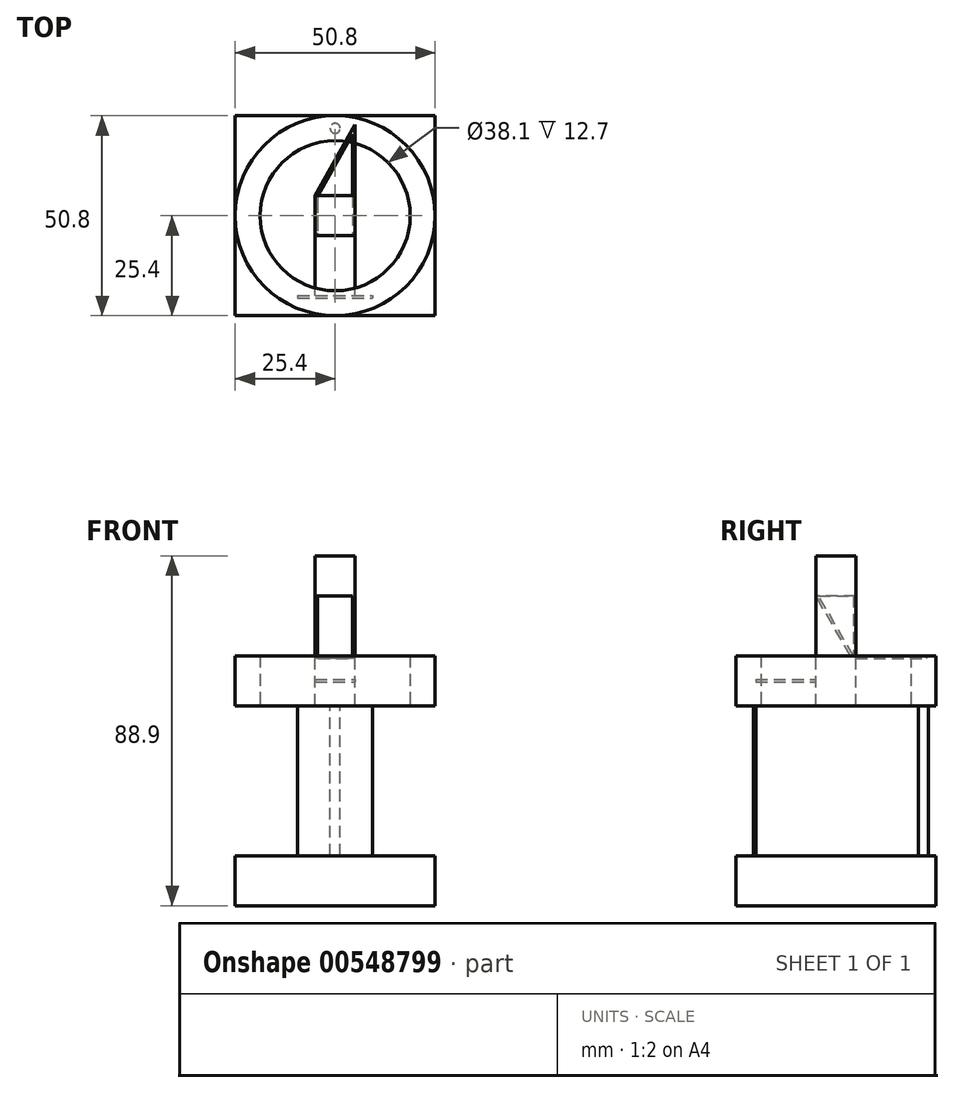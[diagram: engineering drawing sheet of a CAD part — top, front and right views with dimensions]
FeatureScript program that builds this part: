
annotation { "Feature Type Name" : "Feature", "Feature Type Description" : "" }
export const myFeature = defineFeature(function(context is Context, id is Id, definition is map)
    precondition{}
    {
        {
            var Q0;
            Q0=qCreatedBy(makeId("Top.planeOp"),FACE);
            var sketch = newSketch(context, id + "F0", { "sketchPlane" : qUnion([Q0])});
            skLineSegment(sketch, "E0.bottom", {"start": v(-25.4, 25.4) * mm, "end": v(25.4, 25.4) * mm});
            skLineSegment(sketch, "E0.top", {"start": v(-25.4, -25.4) * mm, "end": v(25.4, -25.4) * mm});
            skLineSegment(sketch, "E0.left", {"start": v(-25.4, 25.4) * mm, "end": v(-25.4, -25.4) * mm});
            skLineSegment(sketch, "E0.right", {"start": v(25.4, 25.4) * mm, "end": v(25.4, -25.4) * mm});
            skLineSegment(sketch, "E1", {"start": v(-25.4, -25.4) * mm, "end": v(25.4, 25.4) * mm, "construction": true});
            skSolve(sketch);
        }
        {
            var Q0;
            Q0 = qSketchRegion(id + "F0", true);
            extrude(context, id + "F1", {"entities" : qUnion([Q0]), "depth" : 12.7 * mm, "offsetDistance" : 25.4 * mm});
        }
        {
            var Q0;
            Q0=qCreatedBy(makeId("Top.planeOp"),FACE);
            var sketch = newSketch(context, id + "F2", { "sketchPlane" : qUnion([Q0])});
            skCircle(sketch, "E2", {"center": v(0, 0) * mm, "radius": 25.4 * mm});
            skCircle(sketch, "E3", {"center": v(0, 0) * mm, "radius": 19.05 * mm});
            skSolve(sketch);
        }
        {
            var Q0;
            Q0 = qSketchRegion(id + "F2", true);
            extrude(context, id + "F3", {"entities" : qUnion([Q0]), "operationType" : NewBodyOperationType.ADD, "depth" : 63.5 * mm, "offsetDistance" : 25.4 * mm});
        }
        {
            var Q0;
            Q0=qCreatedBy(makeId("Front.planeOp"),FACE);
            var sketch = newSketch(context, id + "F4", { "sketchPlane" : qUnion([Q0])});
            skLineSegment(sketch, "E4.bottom", {"start": v(35.21, 50.8) * mm, "end": v(-40.99, 50.8) * mm});
            skLineSegment(sketch, "E4.top", {"start": v(35.21, 12.7) * mm, "end": v(-40.99, 12.7) * mm});
            skLineSegment(sketch, "E4.left", {"start": v(35.21, 50.8) * mm, "end": v(35.21, 12.7) * mm});
            skLineSegment(sketch, "E4.right", {"start": v(-40.99, 50.8) * mm, "end": v(-40.99, 12.7) * mm});
            skSolve(sketch);
        }
        {
            var Q0;
            Q0 = qSketchRegion(id + "F4", true);
            extrude(context, id + "F5", {"entities" : qUnion([Q0]), "operationType" : NewBodyOperationType.REMOVE, "endBound" : BoundingType.THROUGH_ALL, "depth" : 25.4 * mm, "offsetDistance" : 25.4 * mm, "hasSecondDirection" : true, "secondDirectionBound" : SecondDirectionBoundingType.THROUGH_ALL, "secondDirectionOppositeDirection" : true, "secondDirectionDepth" : 25.4 * mm});
        }
        {
            var Q0;
            Q0=makeQuery(id+"F5.boolean.opBoolean","COPY",FACE,{"derivedFrom":makeQuery(id+"F5.opExtrude","SWEPT_FACE",FACE,{"disambiguationData":[OSD([sQuery(id+"F4.wireOp",EDGE,"E4.bottom")])]})});
            var sketch = newSketch(context, id + "F6", { "sketchPlane" : qUnion([Q0])});
            skPoint(sketch, "E5", {"position": v(0, 0) * mm});
            skCircle(sketch, "E6", {"center": v(0, -22.23) * mm, "radius": 1.27 * mm});
            skLineSegment(sketch, "E7.bottom", {"start": v(9.53, 20.96) * mm, "end": v(-9.53, 20.96) * mm});
            skLineSegment(sketch, "E7.top", {"start": v(9.53, 20.32) * mm, "end": v(-9.53, 20.32) * mm});
            skLineSegment(sketch, "E7.left", {"start": v(9.52, 20.96) * mm, "end": v(9.52, 20.32) * mm});
            skLineSegment(sketch, "E7.right", {"start": v(-9.53, 20.96) * mm, "end": v(-9.53, 20.32) * mm});
            skLineSegment(sketch, "E8", {"start": v(0, 20.32) * mm, "end": v(0, 0) * mm, "construction": true});
            skSolve(sketch);
        }
        {
            var Q0;
            Q0 = qSketchRegion(id + "F6", true);
            var Q1;
            {var subQ0=sQuery(id+"F0.wireOp",EDGE,"E0.right");var subQ1=sQuery(id+"F0.wireOp",EDGE,"E0.left");var subQ2=sQuery(id+"F0.wireOp",EDGE,"E0.top");var subQ3=sQuery(id+"F0.wireOp",EDGE,"E0.bottom");var subQ4=makeQuery(id+"F1.opExtrude","CAP_FACE",FACE,{"disambiguationData":[OSD([subQ3,subQ2,subQ1,subQ0])],"isStart":false});var subQ5=makeQuery(id+"F1.opExtrude","SWEPT_FACE",FACE,{"disambiguationData":[OSD([subQ2])]});var subQ6=makeQuery(id+"F3.opExtrude","SWEPT_FACE",FACE,{"disambiguationData":[OSD([sQuery(id+"F2.wireOp",EDGE,"E2")])]});var subQ7=makeQuery(id+"F1.opExtrude","SWEPT_FACE",FACE,{"disambiguationData":[OSD([subQ0])]});var subQ8=makeQuery(id+"F1.opExtrude","SWEPT_FACE",FACE,{"disambiguationData":[OSD([subQ1])]});var subQ9=makeQuery(id+"F1.opExtrude","SWEPT_FACE",FACE,{"disambiguationData":[OSD([subQ3])]});Q1=makeQuery(id+"F5.boolean.opBoolean","MERGE",FACE,{"derivedFrom":[makeQuery(id+"F3.boolean.opBoolean","SPLIT",FACE,{"disambiguationData":[TD([makeQuery(id+"F3.opExtrude","SWEPT_FACE",FACE,{"disambiguationData":[OSD([sQuery(id+"F2.wireOp",EDGE,"E3")])]})])],"derivedFrom":subQ4}),makeQuery(id+"F3.boolean.opBoolean","SPLIT",FACE,{"disambiguationData":[TD([subQ9,subQ4,subQ8,subQ6])],"derivedFrom":subQ4}),makeQuery(id+"F3.boolean.opBoolean","SPLIT",FACE,{"disambiguationData":[TD([subQ9,subQ4,subQ7,subQ6])],"derivedFrom":subQ4}),makeQuery(id+"F3.boolean.opBoolean","SPLIT",FACE,{"disambiguationData":[TD([subQ4,subQ5,subQ8,subQ6])],"derivedFrom":subQ4}),makeQuery(id+"F3.boolean.opBoolean","SPLIT",FACE,{"disambiguationData":[TD([subQ4,subQ5,subQ7,subQ6])],"derivedFrom":subQ4}),makeQuery(id+"F5.opExtrude","SWEPT_FACE",FACE,{"disambiguationData":[OSD([sQuery(id+"F4.wireOp",EDGE,"E4.top")])]})]});}
            extrude(context, id + "F7", {"entities" : qUnion([Q0]), "endBound" : BoundingType.UP_TO_SURFACE, "depth" : 25.4 * mm, "endBoundEntityFace" : qUnion([Q1]), "offsetDistance" : 25.4 * mm});
        }
        {
            var Q0;
            Q0=makeQuery(id+"F3.opExtrude","CAP_FACE",FACE,{"disambiguationData":[OSD([sQuery(id+"F2.wireOp",EDGE,"E2"),sQuery(id+"F2.wireOp",EDGE,"E3")])],"isStart":false});
            var sketch = newSketch(context, id + "F8", { "sketchPlane" : qUnion([Q0])});
            skLineSegment(sketch, "E9.bottom", {"start": v(-5.08, 5.08) * mm, "end": v(5.08, 5.08) * mm});
            skLineSegment(sketch, "E9.top", {"start": v(-5.08, -5.08) * mm, "end": v(5.08, -5.08) * mm});
            skLineSegment(sketch, "E9.left", {"start": v(-5.08, 5.08) * mm, "end": v(-5.08, -5.08) * mm});
            skLineSegment(sketch, "E9.right", {"start": v(5.08, 5.08) * mm, "end": v(5.08, -5.08) * mm});
            skLineSegment(sketch, "E10", {"start": v(-5.08, -5.08) * mm, "end": v(5.08, 5.08) * mm, "construction": true});
            skSolve(sketch);
        }
        {
            var Q0;
            Q0 = qSketchRegion(id + "F8", true);
            extrude(context, id + "F9", {"entities" : qUnion([Q0]), "oppositeDirection" : true, "depth" : 12.7 * mm, "offsetDistance" : 25.4 * mm, "hasSecondDirection" : true, "secondDirectionOppositeDirection" : false, "secondDirectionDepth" : 25.4 * mm});
        }
        {
            var Q0;
            Q0=makeQuery(id+"F9.opExtrude","SWEPT_FACE",FACE,{"disambiguationData":[OSD([sQuery(id+"F8.wireOp",EDGE,"E9.right")])]});
            var sketch = newSketch(context, id + "F10", { "sketchPlane" : qUnion([Q0])});
            skLineSegment(sketch, "E11.bottom", {"start": v(-20.32, 57.47) * mm, "end": v(-5.08, 57.47) * mm});
            skLineSegment(sketch, "E11.top", {"start": v(-20.32, 56.83) * mm, "end": v(-5.08, 56.83) * mm});
            skLineSegment(sketch, "E11.left", {"start": v(-20.32, 57.47) * mm, "end": v(-20.32, 56.83) * mm});
            skLineSegment(sketch, "E11.right", {"start": v(-5.08, 57.47) * mm, "end": v(-5.08, 56.83) * mm});
            skLineSegment(sketch, "E12", {"start": v(-5.08, 57.15) * mm, "end": v(-5.08, 50.8) * mm, "construction": true});
            skSolve(sketch);
        }
        {
            var Q0;
            Q0 = qSketchRegion(id + "F10", true);
            var Q1;
            Q1=makeQuery(id+"F9.opExtrude","SWEPT_FACE",FACE,{"disambiguationData":[OSD([sQuery(id+"F8.wireOp",EDGE,"E9.left")])]});
            extrude(context, id + "F11", {"entities" : qUnion([Q0]), "endBound" : BoundingType.UP_TO_SURFACE, "oppositeDirection" : true, "depth" : 25.4 * mm, "endBoundEntityFace" : qUnion([Q1]), "offsetDistance" : 25.4 * mm});
        }
        {
            var Q0;
            Q0=makeQuery(id+"F9.opExtrude","SWEPT_FACE",FACE,{"disambiguationData":[OSD([sQuery(id+"F8.wireOp",EDGE,"E9.top")])]});
            var sketch = newSketch(context, id + "F12", { "sketchPlane" : qUnion([Q0])});
            skLineSegment(sketch, "E13.bottom", {"start": v(-4.45, 78.74) * mm, "end": v(4.45, 78.74) * mm});
            skLineSegment(sketch, "E13.top", {"start": v(-4.44, 63.5) * mm, "end": v(4.45, 63.5) * mm});
            skLineSegment(sketch, "E13.left", {"start": v(-4.45, 78.74) * mm, "end": v(-4.45, 63.5) * mm});
            skLineSegment(sketch, "E13.right", {"start": v(4.45, 78.74) * mm, "end": v(4.45, 63.5) * mm});
            skSolve(sketch);
        }
        {
            var Q0;
            Q0 = qSketchRegion(id + "F12", true);
            var Q1;
            Q1=makeQuery(id+"F9.opExtrude","SWEPT_FACE",FACE,{"disambiguationData":[OSD([sQuery(id+"F8.wireOp",EDGE,"E9.bottom")])]});
            extrude(context, id + "F13", {"entities" : qUnion([Q0]), "operationType" : NewBodyOperationType.REMOVE, "endBound" : BoundingType.UP_TO_SURFACE, "oppositeDirection" : true, "depth" : 9.9 * mm, "endBoundEntityFace" : qUnion([Q1]), "offsetDistance" : 25.4 * mm});
        }
        {
            var Q0;
            Q0=makeQuery(id+"F13.boolean.opBoolean","COPY",FACE,{"derivedFrom":makeQuery(id+"F13.opExtrude","SWEPT_FACE",FACE,{"disambiguationData":[OSD([sQuery(id+"F12.wireOp",EDGE,"E13.top")])]})});
            var sketch = newSketch(context, id + "F14", { "sketchPlane" : qUnion([Q0])});
            skLineSegment(sketch, "E14.bottom", {"start": v(5.08, 5.08) * mm, "end": v(4.45, 5.08) * mm});
            skLineSegment(sketch, "E14.left", {"start": v(5.08, 5.08) * mm, "end": v(5.08, 23.15) * mm});
            skLineSegment(sketch, "E14.right", {"start": v(4.45, 5.08) * mm, "end": v(4.45, 20.72) * mm});
            skLineSegment(sketch, "E15", {"start": v(-5.08, 5.08) * mm, "end": v(-4.35, 5.08) * mm});
            skLineSegment(sketch, "E16", {"start": v(-4.35, 5.08) * mm, "end": v(4.44, 20.72) * mm});
            skLineSegment(sketch, "E17", {"start": v(5.08, 23.15) * mm, "end": v(-5.08, 5.08) * mm});
            skSolve(sketch);
        }
        {
            var Q0;
            Q0 = qSketchRegion(id + "F14", true);
            extrude(context, id + "F15", {"entities" : qUnion([Q0]), "oppositeDirection" : true, "depth" : 0.64 * mm, "offsetDistance" : 25.4 * mm});
        }
        {
            var Q0;
            Q0=makeQuery(id+"F13.boolean.opBoolean","COPY",FACE,{"derivedFrom":makeQuery(id+"F13.opExtrude","SWEPT_FACE",FACE,{"disambiguationData":[OSD([sQuery(id+"F12.wireOp",EDGE,"E13.left")])]})});
            var sketch = newSketch(context, id + "F16", { "sketchPlane" : qUnion([Q0])});
            skLineSegment(sketch, "E18", {"start": v(4.44, 78.74) * mm, "end": v(4.44, 63.5) * mm});
            skLineSegment(sketch, "E19", {"start": v(4.45, 63.5) * mm, "end": v(-4.35, 78.74) * mm});
            skLineSegment(sketch, "E20", {"start": v(-4.35, 78.74) * mm, "end": v(4.44, 78.74) * mm});
            skLineSegment(sketch, "E21", {"start": v(3.71, 63.5) * mm, "end": v(-5.08, 78.74) * mm});
            skLineSegment(sketch, "E22", {"start": v(-5.08, 78.74) * mm, "end": v(-5.08, 63.5) * mm});
            skLineSegment(sketch, "E23", {"start": v(-5.08, 63.5) * mm, "end": v(3.71, 63.5) * mm});
            skSolve(sketch);
        }
        {
            var Q0;
            Q0 = qSketchRegion(id + "F16", true);
            extrude(context, id + "F17", {"entities" : qUnion([Q0]), "operationType" : NewBodyOperationType.REMOVE, "oppositeDirection" : true, "depth" : 5.56 * mm, "offsetDistance" : 25.4 * mm});
        }
    });
